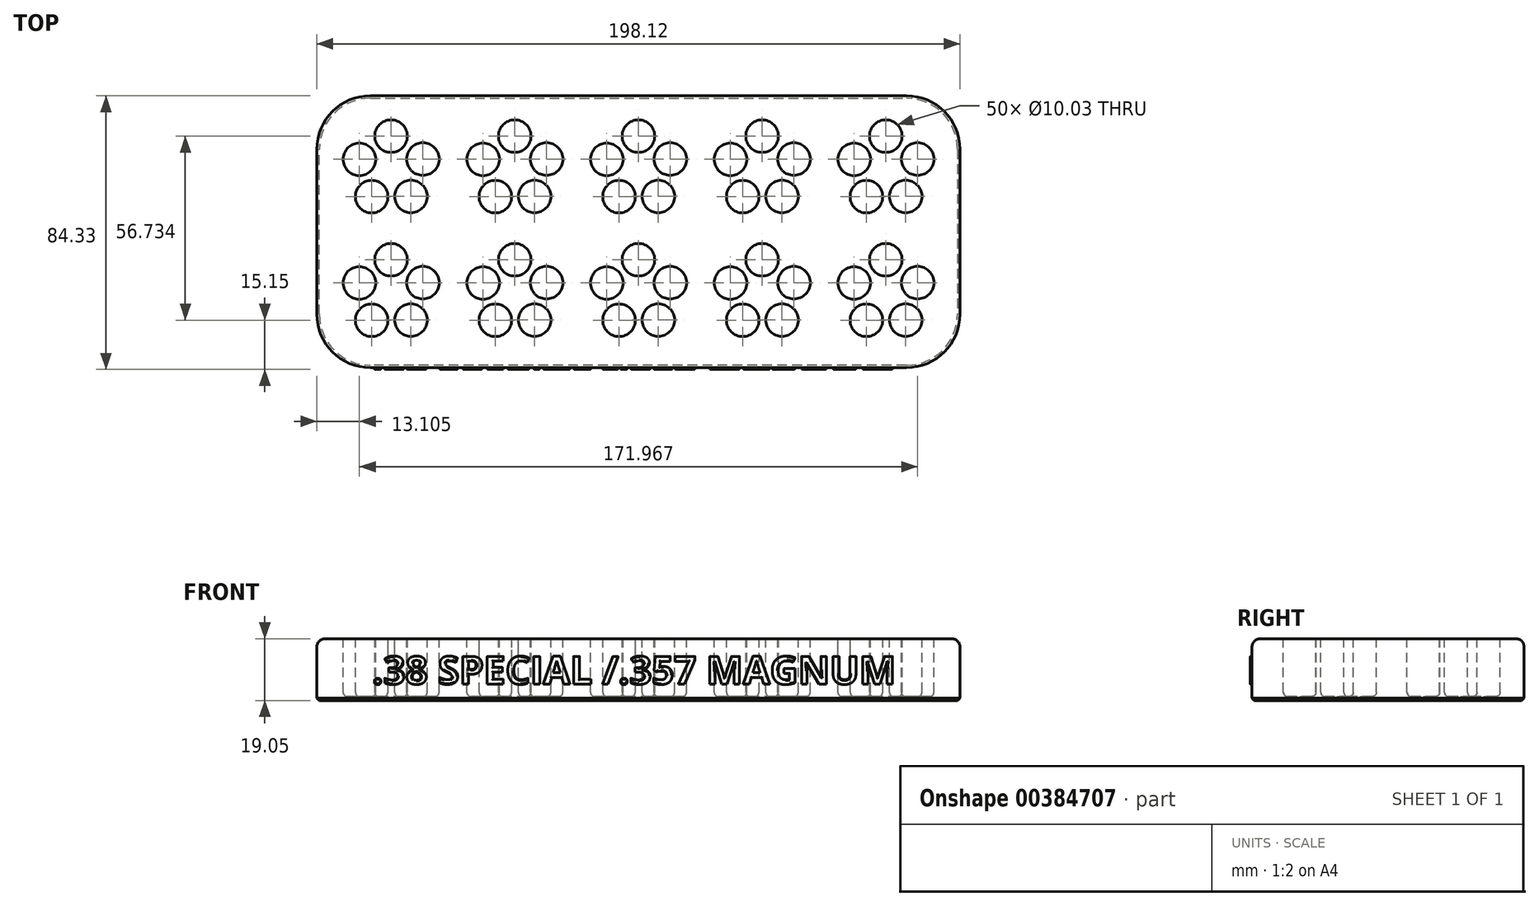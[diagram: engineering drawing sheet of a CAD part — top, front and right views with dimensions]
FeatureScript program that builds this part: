
annotation { "Feature Type Name" : "Feature", "Feature Type Description" : "" }
export const myFeature = defineFeature(function(context is Context, id is Id, definition is map)
    precondition{}
    {
        {
            var Q0;
            Q0=qCreatedBy(makeId("Top.planeOp"),FACE);
            var sketch = newSketch(context, id + "F0", { "sketchPlane" : qUnion([Q0])});
            skLineSegment(sketch, "E0.bottom", {"start": v(-96.52, 50.8) * mm, "end": v(101.6, 50.8) * mm});
            skLineSegment(sketch, "E0.top", {"start": v(-96.52, -33.02) * mm, "end": v(101.6, -33.02) * mm});
            skLineSegment(sketch, "E0.left", {"start": v(-96.52, 50.8) * mm, "end": v(-96.52, -33.02) * mm});
            skLineSegment(sketch, "E0.right", {"start": v(101.6, 50.8) * mm, "end": v(101.6, -33.02) * mm});
            skSolve(sketch);
        }
        {
            var Q0;
            Q0 = qSketchRegion(id + "F0", true);
            extrude(context, id + "F1", {"entities" : qUnion([Q0]), "depth" : 19.05 * mm});
        }
        {
            var Q0;
            Q0=makeQuery(id+"F1.opExtrude","CAP_FACE",FACE,{"disambiguationData":[OSD([sQuery(id+"F0.wireOp",EDGE,"E0.bottom"),sQuery(id+"F0.wireOp",EDGE,"E0.top"),sQuery(id+"F0.wireOp",EDGE,"E0.left"),sQuery(id+"F0.wireOp",EDGE,"E0.right")])],"isStart":false});
            var sketch = newSketch(context, id + "F2", { "sketchPlane" : qUnion([Q0])});
            skCircle(sketch, "E1", {"center": v(-73.66, 27.94) * mm, "radius": 16.83 * mm});
            skCircle(sketch, "E2", {"center": v(-73.66, -10.16) * mm, "radius": 16.83 * mm});
            skCircle(sketch, "E3.1.0.0", {"center": v(-35.56, -10.16) * mm, "radius": 16.83 * mm});
            skCircle(sketch, "E3.1.0.1", {"center": v(-35.56, 27.94) * mm, "radius": 16.83 * mm});
            skCircle(sketch, "E3.2.0.0", {"center": v(2.54, -10.16) * mm, "radius": 16.83 * mm});
            skCircle(sketch, "E3.2.0.1", {"center": v(2.54, 27.94) * mm, "radius": 16.83 * mm});
            skCircle(sketch, "E3.3.0.0", {"center": v(40.64, -10.16) * mm, "radius": 16.83 * mm});
            skCircle(sketch, "E3.3.0.1", {"center": v(40.64, 27.94) * mm, "radius": 16.83 * mm});
            skCircle(sketch, "E3.4.0.0", {"center": v(78.74, -10.16) * mm, "radius": 16.83 * mm});
            skCircle(sketch, "E3.4.0.1", {"center": v(78.74, 27.94) * mm, "radius": 16.83 * mm});
            skLineSegment(sketch, "E3.direction1", {"start": v(-73.66, -10.16) * mm, "end": v(-35.56, -10.16) * mm, "construction": true});
            skSolve(sketch);
        }
        {
            var Q0;
            Q0=makeQuery(id+"F2.imprint","IMPRINT",FACE,{"disambiguationData":[TD([[makeQuery(id+"F2.imprint","IMPRINT",EDGE,{"derivedFrom":sQuery(id+"F2.wireOp",EDGE,"E1")}),-1.0]])]});
            var sketch = newSketch(context, id + "F3", { "sketchPlane" : qUnion([Q0])});
            skCircle(sketch, "E4", {"center": v(-73.66, 38.35) * mm, "radius": 5.02 * mm});
            skCircle(sketch, "E5.1.0", {"center": v(-83.42, 31.2) * mm, "radius": 5.02 * mm});
            skCircle(sketch, "E5.2.0", {"center": v(-79.63, 19.72) * mm, "radius": 5.02 * mm});
            skCircle(sketch, "E5.3.0", {"center": v(-67.54, 19.77) * mm, "radius": 5.02 * mm});
            skCircle(sketch, "E5.4.0", {"center": v(-63.85, 31.29) * mm, "radius": 5.02 * mm});
            skPoint(sketch, "E5.center", {"position": v(-73.62, 28.07) * mm});
            skCircle(sketch, "E6.0.1.0", {"center": v(-79.63, -18.38) * mm, "radius": 5.02 * mm});
            skPoint(sketch, "E6.0.1.1", {"position": v(-73.62, -10.03) * mm});
            skCircle(sketch, "E6.0.1.2", {"center": v(-67.54, -18.33) * mm, "radius": 5.02 * mm});
            skCircle(sketch, "E6.0.1.3", {"center": v(-63.85, -6.81) * mm, "radius": 5.02 * mm});
            skCircle(sketch, "E6.0.1.4", {"center": v(-83.42, -6.9) * mm, "radius": 5.02 * mm});
            skCircle(sketch, "E6.0.1.5", {"center": v(-73.66, 0.25) * mm, "radius": 5.02 * mm});
            skCircle(sketch, "E6.1.0.0", {"center": v(-41.53, 19.72) * mm, "radius": 5.02 * mm});
            skPoint(sketch, "E6.1.0.1", {"position": v(-35.52, 28.07) * mm});
            skCircle(sketch, "E6.1.0.2", {"center": v(-29.44, 19.77) * mm, "radius": 5.02 * mm});
            skCircle(sketch, "E6.1.0.3", {"center": v(-25.75, 31.29) * mm, "radius": 5.02 * mm});
            skCircle(sketch, "E6.1.0.4", {"center": v(-45.32, 31.2) * mm, "radius": 5.02 * mm});
            skCircle(sketch, "E6.1.0.5", {"center": v(-35.56, 38.35) * mm, "radius": 5.02 * mm});
            skCircle(sketch, "E6.1.1.0", {"center": v(-41.53, -18.38) * mm, "radius": 5.02 * mm});
            skPoint(sketch, "E6.1.1.1", {"position": v(-35.52, -10.03) * mm});
            skCircle(sketch, "E6.1.1.2", {"center": v(-29.44, -18.33) * mm, "radius": 5.02 * mm});
            skCircle(sketch, "E6.1.1.3", {"center": v(-25.75, -6.81) * mm, "radius": 5.02 * mm});
            skCircle(sketch, "E6.1.1.4", {"center": v(-45.32, -6.9) * mm, "radius": 5.02 * mm});
            skCircle(sketch, "E6.1.1.5", {"center": v(-35.56, 0.25) * mm, "radius": 5.02 * mm});
            skCircle(sketch, "E6.2.0.0", {"center": v(-3.43, 19.72) * mm, "radius": 5.02 * mm});
            skPoint(sketch, "E6.2.0.1", {"position": v(2.58, 28.07) * mm});
            skCircle(sketch, "E6.2.0.2", {"center": v(8.66, 19.77) * mm, "radius": 5.02 * mm});
            skCircle(sketch, "E6.2.0.3", {"center": v(12.35, 31.29) * mm, "radius": 5.02 * mm});
            skCircle(sketch, "E6.2.0.4", {"center": v(-7.22, 31.2) * mm, "radius": 5.02 * mm});
            skCircle(sketch, "E6.2.0.5", {"center": v(2.54, 38.35) * mm, "radius": 5.02 * mm});
            skCircle(sketch, "E6.2.1.0", {"center": v(-3.43, -18.38) * mm, "radius": 5.02 * mm});
            skPoint(sketch, "E6.2.1.1", {"position": v(2.58, -10.03) * mm});
            skCircle(sketch, "E6.2.1.2", {"center": v(8.66, -18.33) * mm, "radius": 5.02 * mm});
            skCircle(sketch, "E6.2.1.3", {"center": v(12.35, -6.81) * mm, "radius": 5.02 * mm});
            skCircle(sketch, "E6.2.1.4", {"center": v(-7.22, -6.9) * mm, "radius": 5.02 * mm});
            skCircle(sketch, "E6.2.1.5", {"center": v(2.54, 0.25) * mm, "radius": 5.02 * mm});
            skCircle(sketch, "E6.3.0.0", {"center": v(34.67, 19.72) * mm, "radius": 5.02 * mm});
            skPoint(sketch, "E6.3.0.1", {"position": v(40.68, 28.07) * mm});
            skCircle(sketch, "E6.3.0.2", {"center": v(46.76, 19.77) * mm, "radius": 5.02 * mm});
            skCircle(sketch, "E6.3.0.3", {"center": v(50.45, 31.29) * mm, "radius": 5.02 * mm});
            skCircle(sketch, "E6.3.0.4", {"center": v(30.88, 31.2) * mm, "radius": 5.02 * mm});
            skCircle(sketch, "E6.3.0.5", {"center": v(40.64, 38.35) * mm, "radius": 5.02 * mm});
            skCircle(sketch, "E6.3.1.0", {"center": v(34.67, -18.38) * mm, "radius": 5.02 * mm});
            skPoint(sketch, "E6.3.1.1", {"position": v(40.68, -10.03) * mm});
            skCircle(sketch, "E6.3.1.2", {"center": v(46.76, -18.33) * mm, "radius": 5.02 * mm});
            skCircle(sketch, "E6.3.1.3", {"center": v(50.45, -6.81) * mm, "radius": 5.02 * mm});
            skCircle(sketch, "E6.3.1.4", {"center": v(30.88, -6.9) * mm, "radius": 5.02 * mm});
            skCircle(sketch, "E6.3.1.5", {"center": v(40.64, 0.25) * mm, "radius": 5.02 * mm});
            skCircle(sketch, "E6.4.0.0", {"center": v(72.77, 19.72) * mm, "radius": 5.02 * mm});
            skPoint(sketch, "E6.4.0.1", {"position": v(78.78, 28.07) * mm});
            skCircle(sketch, "E6.4.0.2", {"center": v(84.86, 19.77) * mm, "radius": 5.02 * mm});
            skCircle(sketch, "E6.4.0.3", {"center": v(88.55, 31.29) * mm, "radius": 5.02 * mm});
            skCircle(sketch, "E6.4.0.4", {"center": v(68.98, 31.2) * mm, "radius": 5.02 * mm});
            skCircle(sketch, "E6.4.0.5", {"center": v(78.74, 38.35) * mm, "radius": 5.02 * mm});
            skCircle(sketch, "E6.4.1.0", {"center": v(72.77, -18.38) * mm, "radius": 5.02 * mm});
            skPoint(sketch, "E6.4.1.1", {"position": v(78.78, -10.03) * mm});
            skCircle(sketch, "E6.4.1.2", {"center": v(84.86, -18.33) * mm, "radius": 5.02 * mm});
            skCircle(sketch, "E6.4.1.3", {"center": v(88.55, -6.81) * mm, "radius": 5.02 * mm});
            skCircle(sketch, "E6.4.1.4", {"center": v(68.98, -6.9) * mm, "radius": 5.02 * mm});
            skCircle(sketch, "E6.4.1.5", {"center": v(78.74, 0.25) * mm, "radius": 5.02 * mm});
            skLineSegment(sketch, "E6.direction1", {"start": v(-79.63, 19.72) * mm, "end": v(-41.53, 19.72) * mm, "construction": true});
            skLineSegment(sketch, "E6.direction2", {"start": v(-79.63, 19.72) * mm, "end": v(-79.63, -18.38) * mm, "construction": true});
            skSolve(sketch);
        }
        {
            var Q0;
            Q0 = qSketchRegion(id + "F3", true);
            extrude(context, id + "F4", {"entities" : qUnion([Q0]), "operationType" : NewBodyOperationType.REMOVE, "oppositeDirection" : true, "depth" : 17.78 * mm});
        }
        {
            var Q0;
            Q0=makeQuery(id+"F1.opExtrude","SWEPT_EDGE",EDGE,{"disambiguationData":[OSD([sQuery(id+"F0.wireOp",EDGE,"E0.top"),sQuery(id+"F0.wireOp",EDGE,"E0.left")])]});
            var Q1;
            Q1=makeQuery(id+"F1.opExtrude","SWEPT_EDGE",EDGE,{"disambiguationData":[OSD([sQuery(id+"F0.wireOp",EDGE,"E0.bottom"),sQuery(id+"F0.wireOp",EDGE,"E0.left")])]});
            var Q2;
            Q2=makeQuery(id+"F1.opExtrude","SWEPT_EDGE",EDGE,{"disambiguationData":[OSD([sQuery(id+"F0.wireOp",EDGE,"E0.bottom"),sQuery(id+"F0.wireOp",EDGE,"E0.right")])]});
            var Q3;
            Q3=makeQuery(id+"F1.opExtrude","SWEPT_EDGE",EDGE,{"disambiguationData":[OSD([sQuery(id+"F0.wireOp",EDGE,"E0.top"),sQuery(id+"F0.wireOp",EDGE,"E0.right")])]});
            fillet(context, id + "F5", {"entities" : qUnion([Q0, Q1, Q2, Q3]), "radius" : 16.5 * mm, "tangentPropagation" : true, "allowEdgeOverflow" : false});
        }
        {
            var Q0;
            Q0=makeQuery(id+"F1.opExtrude","CAP_EDGE",EDGE,{"disambiguationData":[OSD([sQuery(id+"F0.wireOp",EDGE,"E0.bottom")])],"isStart":false});
            fillet(context, id + "F6", {"entities" : qUnion([Q0]), "radius" : 2.54 * mm, "tangentPropagation" : true, "allowEdgeOverflow" : false});
        }
        {
            var Q0;
            Q0=makeQuery(id+"F4.boolean.opBoolean","COPY",EDGE,{"derivedFrom":makeQuery(id+"F4.opExtrude","CAP_EDGE",EDGE,{"disambiguationData":[OSD([sQuery(id+"F3.wireOp",EDGE,"E6.2.0.3")])],"isStart":true})});
            var Q1;
            Q1=makeQuery(id+"F4.boolean.opBoolean","COPY",EDGE,{"derivedFrom":makeQuery(id+"F4.opExtrude","CAP_EDGE",EDGE,{"disambiguationData":[OSD([sQuery(id+"F3.wireOp",EDGE,"E6.1.0.3")])],"isStart":true})});
            var Q2;
            Q2=makeQuery(id+"F4.boolean.opBoolean","COPY",EDGE,{"derivedFrom":makeQuery(id+"F4.opExtrude","CAP_EDGE",EDGE,{"disambiguationData":[OSD([sQuery(id+"F3.wireOp",EDGE,"E6.4.0.3")])],"isStart":true})});
            var Q3;
            Q3=makeQuery(id+"F4.boolean.opBoolean","COPY",EDGE,{"derivedFrom":makeQuery(id+"F4.opExtrude","CAP_EDGE",EDGE,{"disambiguationData":[OSD([sQuery(id+"F3.wireOp",EDGE,"E6.4.1.0")])],"isStart":true})});
            var Q4;
            Q4=makeQuery(id+"F4.boolean.opBoolean","COPY",EDGE,{"derivedFrom":makeQuery(id+"F4.opExtrude","CAP_EDGE",EDGE,{"disambiguationData":[OSD([sQuery(id+"F3.wireOp",EDGE,"E6.4.0.2")])],"isStart":true})});
            var Q5;
            Q5=makeQuery(id+"F4.boolean.opBoolean","COPY",EDGE,{"derivedFrom":makeQuery(id+"F4.opExtrude","CAP_EDGE",EDGE,{"disambiguationData":[OSD([sQuery(id+"F3.wireOp",EDGE,"E6.4.0.0")])],"isStart":true})});
            var Q6;
            Q6=makeQuery(id+"F4.boolean.opBoolean","COPY",EDGE,{"derivedFrom":makeQuery(id+"F4.opExtrude","CAP_EDGE",EDGE,{"disambiguationData":[OSD([sQuery(id+"F3.wireOp",EDGE,"E6.0.1.5")])],"isStart":true})});
            var Q7;
            Q7=makeQuery(id+"F4.boolean.opBoolean","COPY",EDGE,{"derivedFrom":makeQuery(id+"F4.opExtrude","CAP_EDGE",EDGE,{"disambiguationData":[OSD([sQuery(id+"F3.wireOp",EDGE,"E6.2.0.0")])],"isStart":true})});
            var Q8;
            Q8=makeQuery(id+"F4.boolean.opBoolean","COPY",EDGE,{"derivedFrom":makeQuery(id+"F4.opExtrude","CAP_EDGE",EDGE,{"disambiguationData":[OSD([sQuery(id+"F3.wireOp",EDGE,"E4")])],"isStart":true})});
            var Q9;
            Q9=makeQuery(id+"F4.boolean.opBoolean","COPY",EDGE,{"derivedFrom":makeQuery(id+"F4.opExtrude","CAP_EDGE",EDGE,{"disambiguationData":[OSD([sQuery(id+"F3.wireOp",EDGE,"E6.2.1.0")])],"isStart":true})});
            var Q10;
            Q10=makeQuery(id+"F4.boolean.opBoolean","COPY",EDGE,{"derivedFrom":makeQuery(id+"F4.opExtrude","CAP_EDGE",EDGE,{"disambiguationData":[OSD([sQuery(id+"F3.wireOp",EDGE,"E6.1.1.3")])],"isStart":true})});
            var Q11;
            Q11=makeQuery(id+"F4.boolean.opBoolean","COPY",EDGE,{"derivedFrom":makeQuery(id+"F4.opExtrude","CAP_EDGE",EDGE,{"disambiguationData":[OSD([sQuery(id+"F3.wireOp",EDGE,"E6.2.1.2")])],"isStart":true})});
            var Q12;
            Q12=makeQuery(id+"F4.boolean.opBoolean","COPY",EDGE,{"derivedFrom":makeQuery(id+"F4.opExtrude","CAP_EDGE",EDGE,{"disambiguationData":[OSD([sQuery(id+"F3.wireOp",EDGE,"E5.4.0")])],"isStart":true})});
            var Q13;
            Q13=makeQuery(id+"F4.boolean.opBoolean","COPY",EDGE,{"derivedFrom":makeQuery(id+"F4.opExtrude","CAP_EDGE",EDGE,{"disambiguationData":[OSD([sQuery(id+"F3.wireOp",EDGE,"E5.3.0")])],"isStart":true})});
            var Q14;
            Q14=makeQuery(id+"F4.boolean.opBoolean","COPY",EDGE,{"derivedFrom":makeQuery(id+"F4.opExtrude","CAP_EDGE",EDGE,{"disambiguationData":[OSD([sQuery(id+"F3.wireOp",EDGE,"E6.3.1.4")])],"isStart":true})});
            var Q15;
            Q15=makeQuery(id+"F4.boolean.opBoolean","COPY",EDGE,{"derivedFrom":makeQuery(id+"F4.opExtrude","CAP_EDGE",EDGE,{"disambiguationData":[OSD([sQuery(id+"F3.wireOp",EDGE,"E6.1.0.5")])],"isStart":true})});
            var Q16;
            Q16=makeQuery(id+"F4.boolean.opBoolean","COPY",EDGE,{"derivedFrom":makeQuery(id+"F4.opExtrude","CAP_EDGE",EDGE,{"disambiguationData":[OSD([sQuery(id+"F3.wireOp",EDGE,"E6.1.0.4")])],"isStart":true})});
            var Q17;
            Q17=makeQuery(id+"F4.boolean.opBoolean","COPY",EDGE,{"derivedFrom":makeQuery(id+"F4.opExtrude","CAP_EDGE",EDGE,{"disambiguationData":[OSD([sQuery(id+"F3.wireOp",EDGE,"E6.2.1.3")])],"isStart":true})});
            var Q18;
            Q18=makeQuery(id+"F4.boolean.opBoolean","COPY",EDGE,{"derivedFrom":makeQuery(id+"F4.opExtrude","CAP_EDGE",EDGE,{"disambiguationData":[OSD([sQuery(id+"F3.wireOp",EDGE,"E6.1.1.4")])],"isStart":true})});
            var Q19;
            Q19=makeQuery(id+"F4.boolean.opBoolean","COPY",EDGE,{"derivedFrom":makeQuery(id+"F4.opExtrude","CAP_EDGE",EDGE,{"disambiguationData":[OSD([sQuery(id+"F3.wireOp",EDGE,"E6.3.0.2")])],"isStart":true})});
            var Q20;
            Q20=makeQuery(id+"F4.boolean.opBoolean","COPY",EDGE,{"derivedFrom":makeQuery(id+"F4.opExtrude","CAP_EDGE",EDGE,{"disambiguationData":[OSD([sQuery(id+"F3.wireOp",EDGE,"E6.3.1.5")])],"isStart":true})});
            var Q21;
            Q21=makeQuery(id+"F4.boolean.opBoolean","COPY",EDGE,{"derivedFrom":makeQuery(id+"F4.opExtrude","CAP_EDGE",EDGE,{"disambiguationData":[OSD([sQuery(id+"F3.wireOp",EDGE,"E6.4.1.3")])],"isStart":true})});
            var Q22;
            Q22=makeQuery(id+"F4.boolean.opBoolean","COPY",EDGE,{"derivedFrom":makeQuery(id+"F4.opExtrude","CAP_EDGE",EDGE,{"disambiguationData":[OSD([sQuery(id+"F3.wireOp",EDGE,"E6.2.1.5")])],"isStart":true})});
            var Q23;
            Q23=makeQuery(id+"F4.boolean.opBoolean","COPY",EDGE,{"derivedFrom":makeQuery(id+"F4.opExtrude","CAP_EDGE",EDGE,{"disambiguationData":[OSD([sQuery(id+"F3.wireOp",EDGE,"E6.4.1.2")])],"isStart":true})});
            var Q24;
            Q24=makeQuery(id+"F4.boolean.opBoolean","COPY",EDGE,{"derivedFrom":makeQuery(id+"F4.opExtrude","CAP_EDGE",EDGE,{"disambiguationData":[OSD([sQuery(id+"F3.wireOp",EDGE,"E6.2.0.2")])],"isStart":true})});
            var Q25;
            Q25=makeQuery(id+"F4.boolean.opBoolean","COPY",EDGE,{"derivedFrom":makeQuery(id+"F4.opExtrude","CAP_EDGE",EDGE,{"disambiguationData":[OSD([sQuery(id+"F3.wireOp",EDGE,"E6.1.1.5")])],"isStart":true})});
            var Q26;
            Q26=makeQuery(id+"F4.boolean.opBoolean","COPY",EDGE,{"derivedFrom":makeQuery(id+"F4.opExtrude","CAP_EDGE",EDGE,{"disambiguationData":[OSD([sQuery(id+"F3.wireOp",EDGE,"E6.3.0.0")])],"isStart":true})});
            var Q27;
            Q27=makeQuery(id+"F4.boolean.opBoolean","COPY",EDGE,{"derivedFrom":makeQuery(id+"F4.opExtrude","CAP_EDGE",EDGE,{"disambiguationData":[OSD([sQuery(id+"F3.wireOp",EDGE,"E6.2.0.5")])],"isStart":true})});
            var Q28;
            Q28=makeQuery(id+"F4.boolean.opBoolean","COPY",EDGE,{"derivedFrom":makeQuery(id+"F4.opExtrude","CAP_EDGE",EDGE,{"disambiguationData":[OSD([sQuery(id+"F3.wireOp",EDGE,"E6.0.1.0")])],"isStart":true})});
            var Q29;
            Q29=makeQuery(id+"F4.boolean.opBoolean","COPY",EDGE,{"derivedFrom":makeQuery(id+"F4.opExtrude","CAP_EDGE",EDGE,{"disambiguationData":[OSD([sQuery(id+"F3.wireOp",EDGE,"E6.4.0.4")])],"isStart":true})});
            var Q30;
            Q30=makeQuery(id+"F4.boolean.opBoolean","COPY",EDGE,{"derivedFrom":makeQuery(id+"F4.opExtrude","CAP_EDGE",EDGE,{"disambiguationData":[OSD([sQuery(id+"F3.wireOp",EDGE,"E6.4.0.5")])],"isStart":true})});
            var Q31;
            Q31=makeQuery(id+"F4.boolean.opBoolean","COPY",EDGE,{"derivedFrom":makeQuery(id+"F4.opExtrude","CAP_EDGE",EDGE,{"disambiguationData":[OSD([sQuery(id+"F3.wireOp",EDGE,"E6.3.0.3")])],"isStart":true})});
            var Q32;
            Q32=makeQuery(id+"F4.boolean.opBoolean","COPY",EDGE,{"derivedFrom":makeQuery(id+"F4.opExtrude","CAP_EDGE",EDGE,{"disambiguationData":[OSD([sQuery(id+"F3.wireOp",EDGE,"E6.4.1.4")])],"isStart":true})});
            var Q33;
            Q33=makeQuery(id+"F4.boolean.opBoolean","COPY",EDGE,{"derivedFrom":makeQuery(id+"F4.opExtrude","CAP_EDGE",EDGE,{"disambiguationData":[OSD([sQuery(id+"F3.wireOp",EDGE,"E6.3.1.2")])],"isStart":true})});
            var Q34;
            Q34=makeQuery(id+"F4.boolean.opBoolean","COPY",EDGE,{"derivedFrom":makeQuery(id+"F4.opExtrude","CAP_EDGE",EDGE,{"disambiguationData":[OSD([sQuery(id+"F3.wireOp",EDGE,"E5.2.0")])],"isStart":true})});
            var Q35;
            Q35=makeQuery(id+"F4.boolean.opBoolean","COPY",EDGE,{"derivedFrom":makeQuery(id+"F4.opExtrude","CAP_EDGE",EDGE,{"disambiguationData":[OSD([sQuery(id+"F3.wireOp",EDGE,"E6.0.1.2")])],"isStart":true})});
            var Q36;
            Q36=makeQuery(id+"F4.boolean.opBoolean","COPY",EDGE,{"derivedFrom":makeQuery(id+"F4.opExtrude","CAP_EDGE",EDGE,{"disambiguationData":[OSD([sQuery(id+"F3.wireOp",EDGE,"E6.1.0.2")])],"isStart":true})});
            var Q37;
            Q37=makeQuery(id+"F4.boolean.opBoolean","COPY",EDGE,{"derivedFrom":makeQuery(id+"F4.opExtrude","CAP_EDGE",EDGE,{"disambiguationData":[OSD([sQuery(id+"F3.wireOp",EDGE,"E6.1.1.0")])],"isStart":true})});
            var Q38;
            Q38=makeQuery(id+"F4.boolean.opBoolean","COPY",EDGE,{"derivedFrom":makeQuery(id+"F4.opExtrude","CAP_EDGE",EDGE,{"disambiguationData":[OSD([sQuery(id+"F3.wireOp",EDGE,"E6.2.0.4")])],"isStart":true})});
            var Q39;
            Q39=makeQuery(id+"F4.boolean.opBoolean","COPY",EDGE,{"derivedFrom":makeQuery(id+"F4.opExtrude","CAP_EDGE",EDGE,{"disambiguationData":[OSD([sQuery(id+"F3.wireOp",EDGE,"E6.2.1.4")])],"isStart":true})});
            var Q40;
            Q40=makeQuery(id+"F4.boolean.opBoolean","COPY",EDGE,{"derivedFrom":makeQuery(id+"F4.opExtrude","CAP_EDGE",EDGE,{"disambiguationData":[OSD([sQuery(id+"F3.wireOp",EDGE,"E6.1.0.0")])],"isStart":true})});
            var Q41;
            Q41=makeQuery(id+"F4.boolean.opBoolean","COPY",EDGE,{"derivedFrom":makeQuery(id+"F4.opExtrude","CAP_EDGE",EDGE,{"disambiguationData":[OSD([sQuery(id+"F3.wireOp",EDGE,"E6.1.1.2")])],"isStart":true})});
            var Q42;
            Q42=makeQuery(id+"F4.boolean.opBoolean","COPY",EDGE,{"derivedFrom":makeQuery(id+"F4.opExtrude","CAP_EDGE",EDGE,{"disambiguationData":[OSD([sQuery(id+"F3.wireOp",EDGE,"E6.0.1.3")])],"isStart":true})});
            var Q43;
            Q43=makeQuery(id+"F4.boolean.opBoolean","COPY",EDGE,{"derivedFrom":makeQuery(id+"F4.opExtrude","CAP_EDGE",EDGE,{"disambiguationData":[OSD([sQuery(id+"F3.wireOp",EDGE,"E6.4.1.5")])],"isStart":true})});
            var Q44;
            Q44=makeQuery(id+"F4.boolean.opBoolean","COPY",EDGE,{"derivedFrom":makeQuery(id+"F4.opExtrude","CAP_EDGE",EDGE,{"disambiguationData":[OSD([sQuery(id+"F3.wireOp",EDGE,"E6.3.0.4")])],"isStart":true})});
            var Q45;
            Q45=makeQuery(id+"F4.boolean.opBoolean","COPY",EDGE,{"derivedFrom":makeQuery(id+"F4.opExtrude","CAP_EDGE",EDGE,{"disambiguationData":[OSD([sQuery(id+"F3.wireOp",EDGE,"E6.3.0.5")])],"isStart":true})});
            var Q46;
            Q46=makeQuery(id+"F4.boolean.opBoolean","COPY",EDGE,{"derivedFrom":makeQuery(id+"F4.opExtrude","CAP_EDGE",EDGE,{"disambiguationData":[OSD([sQuery(id+"F3.wireOp",EDGE,"E6.3.1.0")])],"isStart":true})});
            var Q47;
            Q47=makeQuery(id+"F4.boolean.opBoolean","COPY",EDGE,{"derivedFrom":makeQuery(id+"F4.opExtrude","CAP_EDGE",EDGE,{"disambiguationData":[OSD([sQuery(id+"F3.wireOp",EDGE,"E6.3.1.3")])],"isStart":true})});
            var Q48;
            Q48=makeQuery(id+"F4.boolean.opBoolean","COPY",EDGE,{"derivedFrom":makeQuery(id+"F4.opExtrude","CAP_EDGE",EDGE,{"disambiguationData":[OSD([sQuery(id+"F3.wireOp",EDGE,"E6.0.1.2")])],"isStart":false})});
            var Q49;
            Q49=makeQuery(id+"F4.boolean.opBoolean","COPY",EDGE,{"derivedFrom":makeQuery(id+"F4.opExtrude","CAP_EDGE",EDGE,{"disambiguationData":[OSD([sQuery(id+"F3.wireOp",EDGE,"E6.0.1.3")])],"isStart":false})});
            var Q50;
            Q50=makeQuery(id+"F4.boolean.opBoolean","COPY",EDGE,{"derivedFrom":makeQuery(id+"F4.opExtrude","CAP_EDGE",EDGE,{"disambiguationData":[OSD([sQuery(id+"F3.wireOp",EDGE,"E4")])],"isStart":false})});
            var Q51;
            Q51=makeQuery(id+"F4.boolean.opBoolean","COPY",EDGE,{"derivedFrom":makeQuery(id+"F4.opExtrude","CAP_EDGE",EDGE,{"disambiguationData":[OSD([sQuery(id+"F3.wireOp",EDGE,"E5.2.0")])],"isStart":false})});
            var Q52;
            Q52=makeQuery(id+"F4.boolean.opBoolean","COPY",EDGE,{"derivedFrom":makeQuery(id+"F4.opExtrude","CAP_EDGE",EDGE,{"disambiguationData":[OSD([sQuery(id+"F3.wireOp",EDGE,"E5.3.0")])],"isStart":false})});
            var Q53;
            Q53=makeQuery(id+"F4.boolean.opBoolean","COPY",EDGE,{"derivedFrom":makeQuery(id+"F4.opExtrude","CAP_EDGE",EDGE,{"disambiguationData":[OSD([sQuery(id+"F3.wireOp",EDGE,"E5.4.0")])],"isStart":false})});
            var Q54;
            Q54=makeQuery(id+"F4.boolean.opBoolean","COPY",EDGE,{"derivedFrom":makeQuery(id+"F4.opExtrude","CAP_EDGE",EDGE,{"disambiguationData":[OSD([sQuery(id+"F3.wireOp",EDGE,"E6.0.1.0")])],"isStart":false})});
            var Q55;
            Q55=makeQuery(id+"F4.boolean.opBoolean","COPY",EDGE,{"derivedFrom":makeQuery(id+"F4.opExtrude","CAP_EDGE",EDGE,{"disambiguationData":[OSD([sQuery(id+"F3.wireOp",EDGE,"E6.1.0.5")])],"isStart":false})});
            var Q56;
            Q56=makeQuery(id+"F4.boolean.opBoolean","COPY",EDGE,{"derivedFrom":makeQuery(id+"F4.opExtrude","CAP_EDGE",EDGE,{"disambiguationData":[OSD([sQuery(id+"F3.wireOp",EDGE,"E6.2.0.3")])],"isStart":false})});
            var Q57;
            Q57=makeQuery(id+"F4.boolean.opBoolean","COPY",EDGE,{"derivedFrom":makeQuery(id+"F4.opExtrude","CAP_EDGE",EDGE,{"disambiguationData":[OSD([sQuery(id+"F3.wireOp",EDGE,"E6.3.0.0")])],"isStart":false})});
            var Q58;
            Q58=makeQuery(id+"F4.boolean.opBoolean","COPY",EDGE,{"derivedFrom":makeQuery(id+"F4.opExtrude","CAP_EDGE",EDGE,{"disambiguationData":[OSD([sQuery(id+"F3.wireOp",EDGE,"E6.3.1.4")])],"isStart":false})});
            var Q59;
            Q59=makeQuery(id+"F4.boolean.opBoolean","COPY",EDGE,{"derivedFrom":makeQuery(id+"F4.opExtrude","CAP_EDGE",EDGE,{"disambiguationData":[OSD([sQuery(id+"F3.wireOp",EDGE,"E6.4.1.2")])],"isStart":false})});
            var Q60;
            Q60=makeQuery(id+"F4.boolean.opBoolean","COPY",EDGE,{"derivedFrom":makeQuery(id+"F4.opExtrude","CAP_EDGE",EDGE,{"disambiguationData":[OSD([sQuery(id+"F3.wireOp",EDGE,"E6.1.1.0")])],"isStart":false})});
            var Q61;
            Q61=makeQuery(id+"F4.boolean.opBoolean","COPY",EDGE,{"derivedFrom":makeQuery(id+"F4.opExtrude","CAP_EDGE",EDGE,{"disambiguationData":[OSD([sQuery(id+"F3.wireOp",EDGE,"E6.2.0.4")])],"isStart":false})});
            var Q62;
            Q62=makeQuery(id+"F4.boolean.opBoolean","COPY",EDGE,{"derivedFrom":makeQuery(id+"F4.opExtrude","CAP_EDGE",EDGE,{"disambiguationData":[OSD([sQuery(id+"F3.wireOp",EDGE,"E6.3.0.2")])],"isStart":false})});
            var Q63;
            Q63=makeQuery(id+"F4.boolean.opBoolean","COPY",EDGE,{"derivedFrom":makeQuery(id+"F4.opExtrude","CAP_EDGE",EDGE,{"disambiguationData":[OSD([sQuery(id+"F3.wireOp",EDGE,"E6.3.1.5")])],"isStart":false})});
            var Q64;
            Q64=makeQuery(id+"F4.boolean.opBoolean","COPY",EDGE,{"derivedFrom":makeQuery(id+"F4.opExtrude","CAP_EDGE",EDGE,{"disambiguationData":[OSD([sQuery(id+"F3.wireOp",EDGE,"E6.4.1.3")])],"isStart":false})});
            var Q65;
            Q65=makeQuery(id+"F4.boolean.opBoolean","COPY",EDGE,{"derivedFrom":makeQuery(id+"F4.opExtrude","CAP_EDGE",EDGE,{"disambiguationData":[OSD([sQuery(id+"F3.wireOp",EDGE,"E6.1.1.2")])],"isStart":false})});
            var Q66;
            Q66=makeQuery(id+"F4.boolean.opBoolean","COPY",EDGE,{"derivedFrom":makeQuery(id+"F4.opExtrude","CAP_EDGE",EDGE,{"disambiguationData":[OSD([sQuery(id+"F3.wireOp",EDGE,"E6.2.0.5")])],"isStart":false})});
            var Q67;
            Q67=makeQuery(id+"F4.boolean.opBoolean","COPY",EDGE,{"derivedFrom":makeQuery(id+"F4.opExtrude","CAP_EDGE",EDGE,{"disambiguationData":[OSD([sQuery(id+"F3.wireOp",EDGE,"E6.3.0.3")])],"isStart":false})});
            var Q68;
            Q68=makeQuery(id+"F4.boolean.opBoolean","COPY",EDGE,{"derivedFrom":makeQuery(id+"F4.opExtrude","CAP_EDGE",EDGE,{"disambiguationData":[OSD([sQuery(id+"F3.wireOp",EDGE,"E6.4.0.0")])],"isStart":false})});
            var Q69;
            Q69=makeQuery(id+"F4.boolean.opBoolean","COPY",EDGE,{"derivedFrom":makeQuery(id+"F4.opExtrude","CAP_EDGE",EDGE,{"disambiguationData":[OSD([sQuery(id+"F3.wireOp",EDGE,"E6.4.1.4")])],"isStart":false})});
            var Q70;
            Q70=makeQuery(id+"F4.boolean.opBoolean","COPY",EDGE,{"derivedFrom":makeQuery(id+"F4.opExtrude","CAP_EDGE",EDGE,{"disambiguationData":[OSD([sQuery(id+"F3.wireOp",EDGE,"E6.0.1.5")])],"isStart":false})});
            var Q71;
            Q71=makeQuery(id+"F4.boolean.opBoolean","COPY",EDGE,{"derivedFrom":makeQuery(id+"F4.opExtrude","CAP_EDGE",EDGE,{"disambiguationData":[OSD([sQuery(id+"F3.wireOp",EDGE,"E6.1.1.3")])],"isStart":false})});
            var Q72;
            Q72=makeQuery(id+"F4.boolean.opBoolean","COPY",EDGE,{"derivedFrom":makeQuery(id+"F4.opExtrude","CAP_EDGE",EDGE,{"disambiguationData":[OSD([sQuery(id+"F3.wireOp",EDGE,"E6.2.1.0")])],"isStart":false})});
            var Q73;
            Q73=makeQuery(id+"F4.boolean.opBoolean","COPY",EDGE,{"derivedFrom":makeQuery(id+"F4.opExtrude","CAP_EDGE",EDGE,{"disambiguationData":[OSD([sQuery(id+"F3.wireOp",EDGE,"E6.3.0.4")])],"isStart":false})});
            var Q74;
            Q74=makeQuery(id+"F4.boolean.opBoolean","COPY",EDGE,{"derivedFrom":makeQuery(id+"F4.opExtrude","CAP_EDGE",EDGE,{"disambiguationData":[OSD([sQuery(id+"F3.wireOp",EDGE,"E6.4.0.2")])],"isStart":false})});
            var Q75;
            Q75=makeQuery(id+"F4.boolean.opBoolean","COPY",EDGE,{"derivedFrom":makeQuery(id+"F4.opExtrude","CAP_EDGE",EDGE,{"disambiguationData":[OSD([sQuery(id+"F3.wireOp",EDGE,"E6.4.1.5")])],"isStart":false})});
            var Q76;
            Q76=makeQuery(id+"F4.boolean.opBoolean","COPY",EDGE,{"derivedFrom":makeQuery(id+"F4.opExtrude","CAP_EDGE",EDGE,{"disambiguationData":[OSD([sQuery(id+"F3.wireOp",EDGE,"E6.1.0.0")])],"isStart":false})});
            var Q77;
            Q77=makeQuery(id+"F4.boolean.opBoolean","COPY",EDGE,{"derivedFrom":makeQuery(id+"F4.opExtrude","CAP_EDGE",EDGE,{"disambiguationData":[OSD([sQuery(id+"F3.wireOp",EDGE,"E6.1.1.4")])],"isStart":false})});
            var Q78;
            Q78=makeQuery(id+"F4.boolean.opBoolean","COPY",EDGE,{"derivedFrom":makeQuery(id+"F4.opExtrude","CAP_EDGE",EDGE,{"disambiguationData":[OSD([sQuery(id+"F3.wireOp",EDGE,"E6.2.1.2")])],"isStart":false})});
            var Q79;
            Q79=makeQuery(id+"F4.boolean.opBoolean","COPY",EDGE,{"derivedFrom":makeQuery(id+"F4.opExtrude","CAP_EDGE",EDGE,{"disambiguationData":[OSD([sQuery(id+"F3.wireOp",EDGE,"E6.3.0.5")])],"isStart":false})});
            var Q80;
            Q80=makeQuery(id+"F4.boolean.opBoolean","COPY",EDGE,{"derivedFrom":makeQuery(id+"F4.opExtrude","CAP_EDGE",EDGE,{"disambiguationData":[OSD([sQuery(id+"F3.wireOp",EDGE,"E6.4.0.3")])],"isStart":false})});
            var Q81;
            Q81=makeQuery(id+"F4.boolean.opBoolean","COPY",EDGE,{"derivedFrom":makeQuery(id+"F4.opExtrude","CAP_EDGE",EDGE,{"disambiguationData":[OSD([sQuery(id+"F3.wireOp",EDGE,"E6.1.0.2")])],"isStart":false})});
            var Q82;
            Q82=makeQuery(id+"F4.boolean.opBoolean","COPY",EDGE,{"derivedFrom":makeQuery(id+"F4.opExtrude","CAP_EDGE",EDGE,{"disambiguationData":[OSD([sQuery(id+"F3.wireOp",EDGE,"E6.1.1.5")])],"isStart":false})});
            var Q83;
            Q83=makeQuery(id+"F4.boolean.opBoolean","COPY",EDGE,{"derivedFrom":makeQuery(id+"F4.opExtrude","CAP_EDGE",EDGE,{"disambiguationData":[OSD([sQuery(id+"F3.wireOp",EDGE,"E6.2.1.3")])],"isStart":false})});
            var Q84;
            Q84=makeQuery(id+"F4.boolean.opBoolean","COPY",EDGE,{"derivedFrom":makeQuery(id+"F4.opExtrude","CAP_EDGE",EDGE,{"disambiguationData":[OSD([sQuery(id+"F3.wireOp",EDGE,"E6.3.1.0")])],"isStart":false})});
            var Q85;
            Q85=makeQuery(id+"F4.boolean.opBoolean","COPY",EDGE,{"derivedFrom":makeQuery(id+"F4.opExtrude","CAP_EDGE",EDGE,{"disambiguationData":[OSD([sQuery(id+"F3.wireOp",EDGE,"E6.4.0.4")])],"isStart":false})});
            var Q86;
            Q86=makeQuery(id+"F4.boolean.opBoolean","COPY",EDGE,{"derivedFrom":makeQuery(id+"F4.opExtrude","CAP_EDGE",EDGE,{"disambiguationData":[OSD([sQuery(id+"F3.wireOp",EDGE,"E6.1.0.3")])],"isStart":false})});
            var Q87;
            Q87=makeQuery(id+"F4.boolean.opBoolean","COPY",EDGE,{"derivedFrom":makeQuery(id+"F4.opExtrude","CAP_EDGE",EDGE,{"disambiguationData":[OSD([sQuery(id+"F3.wireOp",EDGE,"E6.2.0.0")])],"isStart":false})});
            var Q88;
            Q88=makeQuery(id+"F4.boolean.opBoolean","COPY",EDGE,{"derivedFrom":makeQuery(id+"F4.opExtrude","CAP_EDGE",EDGE,{"disambiguationData":[OSD([sQuery(id+"F3.wireOp",EDGE,"E6.2.1.4")])],"isStart":false})});
            var Q89;
            Q89=makeQuery(id+"F4.boolean.opBoolean","COPY",EDGE,{"derivedFrom":makeQuery(id+"F4.opExtrude","CAP_EDGE",EDGE,{"disambiguationData":[OSD([sQuery(id+"F3.wireOp",EDGE,"E6.3.1.2")])],"isStart":false})});
            var Q90;
            Q90=makeQuery(id+"F4.boolean.opBoolean","COPY",EDGE,{"derivedFrom":makeQuery(id+"F4.opExtrude","CAP_EDGE",EDGE,{"disambiguationData":[OSD([sQuery(id+"F3.wireOp",EDGE,"E6.4.0.5")])],"isStart":false})});
            var Q91;
            Q91=makeQuery(id+"F4.boolean.opBoolean","COPY",EDGE,{"derivedFrom":makeQuery(id+"F4.opExtrude","CAP_EDGE",EDGE,{"disambiguationData":[OSD([sQuery(id+"F3.wireOp",EDGE,"E6.1.0.4")])],"isStart":false})});
            var Q92;
            Q92=makeQuery(id+"F4.boolean.opBoolean","COPY",EDGE,{"derivedFrom":makeQuery(id+"F4.opExtrude","CAP_EDGE",EDGE,{"disambiguationData":[OSD([sQuery(id+"F3.wireOp",EDGE,"E6.2.0.2")])],"isStart":false})});
            var Q93;
            Q93=makeQuery(id+"F4.boolean.opBoolean","COPY",EDGE,{"derivedFrom":makeQuery(id+"F4.opExtrude","CAP_EDGE",EDGE,{"disambiguationData":[OSD([sQuery(id+"F3.wireOp",EDGE,"E6.2.1.5")])],"isStart":false})});
            var Q94;
            Q94=makeQuery(id+"F4.boolean.opBoolean","COPY",EDGE,{"derivedFrom":makeQuery(id+"F4.opExtrude","CAP_EDGE",EDGE,{"disambiguationData":[OSD([sQuery(id+"F3.wireOp",EDGE,"E6.3.1.3")])],"isStart":false})});
            var Q95;
            Q95=makeQuery(id+"F4.boolean.opBoolean","COPY",EDGE,{"derivedFrom":makeQuery(id+"F4.opExtrude","CAP_EDGE",EDGE,{"disambiguationData":[OSD([sQuery(id+"F3.wireOp",EDGE,"E6.4.1.0")])],"isStart":false})});
            var Q96;
            Q96=makeQuery(id+"F4.boolean.opBoolean","COPY",EDGE,{"derivedFrom":makeQuery(id+"F4.opExtrude","CAP_EDGE",EDGE,{"disambiguationData":[OSD([sQuery(id+"F3.wireOp",EDGE,"E6.0.1.4")])],"isStart":true})});
            var Q97;
            Q97=makeQuery(id+"F4.boolean.opBoolean","COPY",EDGE,{"derivedFrom":makeQuery(id+"F4.opExtrude","CAP_EDGE",EDGE,{"disambiguationData":[OSD([sQuery(id+"F3.wireOp",EDGE,"E5.1.0")])],"isStart":true})});
            var Q98;
            Q98=makeQuery(id+"F4.boolean.opBoolean","COPY",EDGE,{"derivedFrom":makeQuery(id+"F4.opExtrude","CAP_EDGE",EDGE,{"disambiguationData":[OSD([sQuery(id+"F3.wireOp",EDGE,"E6.0.1.4")])],"isStart":false})});
            var Q99;
            Q99=makeQuery(id+"F4.boolean.opBoolean","COPY",EDGE,{"derivedFrom":makeQuery(id+"F4.opExtrude","CAP_EDGE",EDGE,{"disambiguationData":[OSD([sQuery(id+"F3.wireOp",EDGE,"E5.1.0")])],"isStart":false})});
            fillet(context, id + "F7", {"entities" : qUnion([Q0, Q1, Q2, Q3, Q4, Q5, Q6, Q7, Q8, Q9, Q10, Q11, Q12, Q13, Q14, Q15, Q16, Q17, Q18, Q19, Q20, Q21, Q22, Q23, Q24, Q25, Q26, Q27, Q28, Q29, Q30, Q31, Q32, Q33, Q34, Q35, Q36, Q37, Q38, Q39, Q40, Q41, Q42, Q43, Q44, Q45, Q46, Q47, Q48, Q49, Q50, Q51, Q52, Q53, Q54, Q55, Q56, Q57, Q58, Q59, Q60, Q61, Q62, Q63, Q64, Q65, Q66, Q67, Q68, Q69, Q70, Q71, Q72, Q73, Q74, Q75, Q76, Q77, Q78, Q79, Q80, Q81, Q82, Q83, Q84, Q85, Q86, Q87, Q88, Q89, Q90, Q91, Q92, Q93, Q94, Q95, Q96, Q97, Q98, Q99]), "radius" : 1.27 * mm, "tangentPropagation" : true, "allowEdgeOverflow" : false});
        }
        {
            var Q0;
            Q0=makeQuery(id+"F1.opExtrude","CAP_EDGE",EDGE,{"disambiguationData":[OSD([sQuery(id+"F0.wireOp",EDGE,"E0.top")])],"isStart":true});
            chamfer(context, id + "F8", {"entities" : qUnion([Q0]), "width" : 0.76 * mm, "tangentPropagation" : true});
        }
        {
            var Q0;
            Q0=makeQuery(id+"F1.opExtrude","SWEPT_FACE",FACE,{"disambiguationData":[OSD([sQuery(id+"F0.wireOp",EDGE,"E0.top")])]});
            var sketch = newSketch(context, id + "F9", { "sketchPlane" : qUnion([Q0])});
            skText(sketch, "E7", { "text": ".38 SPECIAL /.357 MAGNUM", "fontName": "OpenSans-Bold.ttf"});
            const initialGuessF9  = {"E7": [-0.0795, 0.00503, 1, 0, 0.00864]};
            skSetInitialGuess(sketch, initialGuessF9);
            skSolve(sketch);
        }
        {
            var Q0;
            Q0 = qSketchRegion(id + "F9", true);
            extrude(context, id + "F10", {"entities" : qUnion([Q0]), "operationType" : NewBodyOperationType.ADD, "depth" : 0.5 * mm, "offsetDistance" : 25.4 * mm});
        }
        {
            var Q0;
            Q0=makeQuery(id+"F10.opExtrude","CAP_FACE",FACE,{"disambiguationData":[OSD([sQuery(id+"F9.wireOp",EDGE,"E7.sketch_text.stroke-0"),sQuery(id+"F9.wireOp",EDGE,"E7.sketch_text.stroke-1"),sQuery(id+"F9.wireOp",EDGE,"E7.sketch_text.stroke-2"),sQuery(id+"F9.wireOp",EDGE,"E7.sketch_text.stroke-3"),sQuery(id+"F9.wireOp",EDGE,"E7.sketch_text.stroke-4"),sQuery(id+"F9.wireOp",EDGE,"E7.sketch_text.stroke-5"),sQuery(id+"F9.wireOp",EDGE,"E7.sketch_text.stroke-6"),sQuery(id+"F9.wireOp",EDGE,"E7.sketch_text.stroke-7")])],"isStart":false});
            var Q1;
            Q1=makeQuery(id+"F10.opExtrude","CAP_FACE",FACE,{"disambiguationData":[OSD([sQuery(id+"F9.wireOp",EDGE,"E7.sketch_text.stroke-8"),sQuery(id+"F9.wireOp",EDGE,"E7.sketch_text.stroke-9"),sQuery(id+"F9.wireOp",EDGE,"E7.sketch_text.stroke-10"),sQuery(id+"F9.wireOp",EDGE,"E7.sketch_text.stroke-11"),sQuery(id+"F9.wireOp",EDGE,"E7.sketch_text.stroke-12"),sQuery(id+"F9.wireOp",EDGE,"E7.sketch_text.stroke-13"),sQuery(id+"F9.wireOp",EDGE,"E7.sketch_text.stroke-14"),sQuery(id+"F9.wireOp",EDGE,"E7.sketch_text.stroke-15"),sQuery(id+"F9.wireOp",EDGE,"E7.sketch_text.stroke-16"),sQuery(id+"F9.wireOp",EDGE,"E7.sketch_text.stroke-17"),sQuery(id+"F9.wireOp",EDGE,"E7.sketch_text.stroke-18"),sQuery(id+"F9.wireOp",EDGE,"E7.sketch_text.stroke-19"),sQuery(id+"F9.wireOp",EDGE,"E7.sketch_text.stroke-20"),sQuery(id+"F9.wireOp",EDGE,"E7.sketch_text.stroke-21"),sQuery(id+"F9.wireOp",EDGE,"E7.sketch_text.stroke-22"),sQuery(id+"F9.wireOp",EDGE,"E7.sketch_text.stroke-23"),sQuery(id+"F9.wireOp",EDGE,"E7.sketch_text.stroke-24"),sQuery(id+"F9.wireOp",EDGE,"E7.sketch_text.stroke-25"),sQuery(id+"F9.wireOp",EDGE,"E7.sketch_text.stroke-26"),sQuery(id+"F9.wireOp",EDGE,"E7.sketch_text.stroke-27"),sQuery(id+"F9.wireOp",EDGE,"E7.sketch_text.stroke-28"),sQuery(id+"F9.wireOp",EDGE,"E7.sketch_text.stroke-29"),sQuery(id+"F9.wireOp",EDGE,"E7.sketch_text.stroke-30"),sQuery(id+"F9.wireOp",EDGE,"E7.sketch_text.stroke-31"),sQuery(id+"F9.wireOp",EDGE,"E7.sketch_text.stroke-32"),sQuery(id+"F9.wireOp",EDGE,"E7.sketch_text.stroke-33"),sQuery(id+"F9.wireOp",EDGE,"E7.sketch_text.stroke-34")])],"isStart":false});
            var Q2;
            Q2=makeQuery(id+"F10.opExtrude","CAP_FACE",FACE,{"disambiguationData":[OSD([sQuery(id+"F9.wireOp",EDGE,"E7.sketch_text.stroke-35"),sQuery(id+"F9.wireOp",EDGE,"E7.sketch_text.stroke-36"),sQuery(id+"F9.wireOp",EDGE,"E7.sketch_text.stroke-37"),sQuery(id+"F9.wireOp",EDGE,"E7.sketch_text.stroke-38"),sQuery(id+"F9.wireOp",EDGE,"E7.sketch_text.stroke-39"),sQuery(id+"F9.wireOp",EDGE,"E7.sketch_text.stroke-40"),sQuery(id+"F9.wireOp",EDGE,"E7.sketch_text.stroke-41"),sQuery(id+"F9.wireOp",EDGE,"E7.sketch_text.stroke-42"),sQuery(id+"F9.wireOp",EDGE,"E7.sketch_text.stroke-43"),sQuery(id+"F9.wireOp",EDGE,"E7.sketch_text.stroke-44"),sQuery(id+"F9.wireOp",EDGE,"E7.sketch_text.stroke-45"),sQuery(id+"F9.wireOp",EDGE,"E7.sketch_text.stroke-46"),sQuery(id+"F9.wireOp",EDGE,"E7.sketch_text.stroke-47"),sQuery(id+"F9.wireOp",EDGE,"E7.sketch_text.stroke-48"),sQuery(id+"F9.wireOp",EDGE,"E7.sketch_text.stroke-49"),sQuery(id+"F9.wireOp",EDGE,"E7.sketch_text.stroke-50"),sQuery(id+"F9.wireOp",EDGE,"E7.sketch_text.stroke-51"),sQuery(id+"F9.wireOp",EDGE,"E7.sketch_text.stroke-52"),sQuery(id+"F9.wireOp",EDGE,"E7.sketch_text.stroke-53"),sQuery(id+"F9.wireOp",EDGE,"E7.sketch_text.stroke-54"),sQuery(id+"F9.wireOp",EDGE,"E7.sketch_text.stroke-55"),sQuery(id+"F9.wireOp",EDGE,"E7.sketch_text.stroke-56"),sQuery(id+"F9.wireOp",EDGE,"E7.sketch_text.stroke-57"),sQuery(id+"F9.wireOp",EDGE,"E7.sketch_text.stroke-58"),sQuery(id+"F9.wireOp",EDGE,"E7.sketch_text.stroke-59"),sQuery(id+"F9.wireOp",EDGE,"E7.sketch_text.stroke-60"),sQuery(id+"F9.wireOp",EDGE,"E7.sketch_text.stroke-61"),sQuery(id+"F9.wireOp",EDGE,"E7.sketch_text.stroke-62"),sQuery(id+"F9.wireOp",EDGE,"E7.sketch_text.stroke-63"),sQuery(id+"F9.wireOp",EDGE,"E7.sketch_text.stroke-64"),sQuery(id+"F9.wireOp",EDGE,"E7.sketch_text.stroke-65")])],"isStart":false});
            var Q3;
            Q3=makeQuery(id+"F10.opExtrude","CAP_FACE",FACE,{"disambiguationData":[OSD([sQuery(id+"F9.wireOp",EDGE,"E7.sketch_text.stroke-66"),sQuery(id+"F9.wireOp",EDGE,"E7.sketch_text.stroke-67"),sQuery(id+"F9.wireOp",EDGE,"E7.sketch_text.stroke-68"),sQuery(id+"F9.wireOp",EDGE,"E7.sketch_text.stroke-69"),sQuery(id+"F9.wireOp",EDGE,"E7.sketch_text.stroke-70"),sQuery(id+"F9.wireOp",EDGE,"E7.sketch_text.stroke-71"),sQuery(id+"F9.wireOp",EDGE,"E7.sketch_text.stroke-72"),sQuery(id+"F9.wireOp",EDGE,"E7.sketch_text.stroke-73"),sQuery(id+"F9.wireOp",EDGE,"E7.sketch_text.stroke-74"),sQuery(id+"F9.wireOp",EDGE,"E7.sketch_text.stroke-75"),sQuery(id+"F9.wireOp",EDGE,"E7.sketch_text.stroke-76"),sQuery(id+"F9.wireOp",EDGE,"E7.sketch_text.stroke-77"),sQuery(id+"F9.wireOp",EDGE,"E7.sketch_text.stroke-78"),sQuery(id+"F9.wireOp",EDGE,"E7.sketch_text.stroke-79"),sQuery(id+"F9.wireOp",EDGE,"E7.sketch_text.stroke-80"),sQuery(id+"F9.wireOp",EDGE,"E7.sketch_text.stroke-81"),sQuery(id+"F9.wireOp",EDGE,"E7.sketch_text.stroke-82"),sQuery(id+"F9.wireOp",EDGE,"E7.sketch_text.stroke-83"),sQuery(id+"F9.wireOp",EDGE,"E7.sketch_text.stroke-84"),sQuery(id+"F9.wireOp",EDGE,"E7.sketch_text.stroke-85"),sQuery(id+"F9.wireOp",EDGE,"E7.sketch_text.stroke-86"),sQuery(id+"F9.wireOp",EDGE,"E7.sketch_text.stroke-87"),sQuery(id+"F9.wireOp",EDGE,"E7.sketch_text.stroke-88"),sQuery(id+"F9.wireOp",EDGE,"E7.sketch_text.stroke-89"),sQuery(id+"F9.wireOp",EDGE,"E7.sketch_text.stroke-90"),sQuery(id+"F9.wireOp",EDGE,"E7.sketch_text.stroke-91"),sQuery(id+"F9.wireOp",EDGE,"E7.sketch_text.stroke-92"),sQuery(id+"F9.wireOp",EDGE,"E7.sketch_text.stroke-93")])],"isStart":false});
            var Q4;
            Q4=makeQuery(id+"F10.opExtrude","CAP_FACE",FACE,{"disambiguationData":[OSD([sQuery(id+"F9.wireOp",EDGE,"E7.sketch_text.stroke-94"),sQuery(id+"F9.wireOp",EDGE,"E7.sketch_text.stroke-95"),sQuery(id+"F9.wireOp",EDGE,"E7.sketch_text.stroke-96"),sQuery(id+"F9.wireOp",EDGE,"E7.sketch_text.stroke-97"),sQuery(id+"F9.wireOp",EDGE,"E7.sketch_text.stroke-98"),sQuery(id+"F9.wireOp",EDGE,"E7.sketch_text.stroke-99"),sQuery(id+"F9.wireOp",EDGE,"E7.sketch_text.stroke-100"),sQuery(id+"F9.wireOp",EDGE,"E7.sketch_text.stroke-101"),sQuery(id+"F9.wireOp",EDGE,"E7.sketch_text.stroke-102"),sQuery(id+"F9.wireOp",EDGE,"E7.sketch_text.stroke-103"),sQuery(id+"F9.wireOp",EDGE,"E7.sketch_text.stroke-104"),sQuery(id+"F9.wireOp",EDGE,"E7.sketch_text.stroke-105"),sQuery(id+"F9.wireOp",EDGE,"E7.sketch_text.stroke-106"),sQuery(id+"F9.wireOp",EDGE,"E7.sketch_text.stroke-107"),sQuery(id+"F9.wireOp",EDGE,"E7.sketch_text.stroke-108"),sQuery(id+"F9.wireOp",EDGE,"E7.sketch_text.stroke-109")])],"isStart":false});
            var Q5;
            Q5=makeQuery(id+"F10.opExtrude","CAP_FACE",FACE,{"disambiguationData":[OSD([sQuery(id+"F9.wireOp",EDGE,"E7.sketch_text.stroke-110"),sQuery(id+"F9.wireOp",EDGE,"E7.sketch_text.stroke-111"),sQuery(id+"F9.wireOp",EDGE,"E7.sketch_text.stroke-112"),sQuery(id+"F9.wireOp",EDGE,"E7.sketch_text.stroke-113"),sQuery(id+"F9.wireOp",EDGE,"E7.sketch_text.stroke-114"),sQuery(id+"F9.wireOp",EDGE,"E7.sketch_text.stroke-115"),sQuery(id+"F9.wireOp",EDGE,"E7.sketch_text.stroke-116"),sQuery(id+"F9.wireOp",EDGE,"E7.sketch_text.stroke-117"),sQuery(id+"F9.wireOp",EDGE,"E7.sketch_text.stroke-118"),sQuery(id+"F9.wireOp",EDGE,"E7.sketch_text.stroke-119"),sQuery(id+"F9.wireOp",EDGE,"E7.sketch_text.stroke-120"),sQuery(id+"F9.wireOp",EDGE,"E7.sketch_text.stroke-121")])],"isStart":false});
            var Q6;
            Q6=makeQuery(id+"F10.opExtrude","CAP_FACE",FACE,{"disambiguationData":[OSD([sQuery(id+"F9.wireOp",EDGE,"E7.sketch_text.stroke-137"),sQuery(id+"F9.wireOp",EDGE,"E7.sketch_text.stroke-138"),sQuery(id+"F9.wireOp",EDGE,"E7.sketch_text.stroke-139"),sQuery(id+"F9.wireOp",EDGE,"E7.sketch_text.stroke-140")])],"isStart":false});
            var Q7;
            Q7=makeQuery(id+"F10.opExtrude","CAP_FACE",FACE,{"disambiguationData":[OSD([sQuery(id+"F9.wireOp",EDGE,"E7.sketch_text.stroke-122"),sQuery(id+"F9.wireOp",EDGE,"E7.sketch_text.stroke-123"),sQuery(id+"F9.wireOp",EDGE,"E7.sketch_text.stroke-124"),sQuery(id+"F9.wireOp",EDGE,"E7.sketch_text.stroke-125"),sQuery(id+"F9.wireOp",EDGE,"E7.sketch_text.stroke-126"),sQuery(id+"F9.wireOp",EDGE,"E7.sketch_text.stroke-127"),sQuery(id+"F9.wireOp",EDGE,"E7.sketch_text.stroke-128"),sQuery(id+"F9.wireOp",EDGE,"E7.sketch_text.stroke-129"),sQuery(id+"F9.wireOp",EDGE,"E7.sketch_text.stroke-130"),sQuery(id+"F9.wireOp",EDGE,"E7.sketch_text.stroke-131"),sQuery(id+"F9.wireOp",EDGE,"E7.sketch_text.stroke-132"),sQuery(id+"F9.wireOp",EDGE,"E7.sketch_text.stroke-133"),sQuery(id+"F9.wireOp",EDGE,"E7.sketch_text.stroke-134"),sQuery(id+"F9.wireOp",EDGE,"E7.sketch_text.stroke-135"),sQuery(id+"F9.wireOp",EDGE,"E7.sketch_text.stroke-136")])],"isStart":false});
            fillet(context, id + "F11", {"entities" : qUnion([Q0, Q1, Q2, Q3, Q4, Q5, Q6, Q7]), "radius" : 0.25 * mm, "tangentPropagation" : true, "allowEdgeOverflow" : false});
        }
        {
            var Q0;
            Q0=makeQuery(id+"F10.opExtrude","CAP_EDGE",EDGE,{"disambiguationData":[OSD([sQuery(id+"F9.wireOp",EDGE,"E7.sketch_text.stroke-145")])],"isStart":false});
            var Q1;
            Q1=makeQuery(id+"F10.opExtrude","CAP_EDGE",EDGE,{"disambiguationData":[OSD([sQuery(id+"F9.wireOp",EDGE,"E7.sketch_text.stroke-146")])],"isStart":false});
            var Q2;
            Q2=makeQuery(id+"F10.opExtrude","CAP_EDGE",EDGE,{"disambiguationData":[OSD([sQuery(id+"F9.wireOp",EDGE,"E7.sketch_text.stroke-147")])],"isStart":false});
            var Q3;
            Q3=makeQuery(id+"F10.opExtrude","CAP_EDGE",EDGE,{"disambiguationData":[OSD([sQuery(id+"F9.wireOp",EDGE,"E7.sketch_text.stroke-148")])],"isStart":false});
            var Q4;
            Q4=makeQuery(id+"F10.opExtrude","CAP_EDGE",EDGE,{"disambiguationData":[OSD([sQuery(id+"F9.wireOp",EDGE,"E7.sketch_text.stroke-141")])],"isStart":false});
            var Q5;
            Q5=makeQuery(id+"F10.opExtrude","CAP_EDGE",EDGE,{"disambiguationData":[OSD([sQuery(id+"F9.wireOp",EDGE,"E7.sketch_text.stroke-142")])],"isStart":false});
            var Q6;
            Q6=makeQuery(id+"F10.opExtrude","CAP_EDGE",EDGE,{"disambiguationData":[OSD([sQuery(id+"F9.wireOp",EDGE,"E7.sketch_text.stroke-143")])],"isStart":false});
            var Q7;
            Q7=makeQuery(id+"F10.opExtrude","CAP_EDGE",EDGE,{"disambiguationData":[OSD([sQuery(id+"F9.wireOp",EDGE,"E7.sketch_text.stroke-144")])],"isStart":false});
            var Q8;
            Q8=makeQuery(id+"F10.opExtrude","CAP_FACE",FACE,{"disambiguationData":[OSD([sQuery(id+"F9.wireOp",EDGE,"E7.sketch_text.stroke-153"),sQuery(id+"F9.wireOp",EDGE,"E7.sketch_text.stroke-154"),sQuery(id+"F9.wireOp",EDGE,"E7.sketch_text.stroke-155"),sQuery(id+"F9.wireOp",EDGE,"E7.sketch_text.stroke-156"),sQuery(id+"F9.wireOp",EDGE,"E7.sketch_text.stroke-157"),sQuery(id+"F9.wireOp",EDGE,"E7.sketch_text.stroke-158")])],"isStart":false});
            var Q9;
            Q9=makeQuery(id+"F10.opExtrude","CAP_FACE",FACE,{"disambiguationData":[OSD([sQuery(id+"F9.wireOp",EDGE,"E7.sketch_text.stroke-159"),sQuery(id+"F9.wireOp",EDGE,"E7.sketch_text.stroke-160"),sQuery(id+"F9.wireOp",EDGE,"E7.sketch_text.stroke-161"),sQuery(id+"F9.wireOp",EDGE,"E7.sketch_text.stroke-162")])],"isStart":false});
            var Q10;
            Q10=makeQuery(id+"F10.opExtrude","CAP_FACE",FACE,{"disambiguationData":[OSD([sQuery(id+"F9.wireOp",EDGE,"E7.sketch_text.stroke-163"),sQuery(id+"F9.wireOp",EDGE,"E7.sketch_text.stroke-164"),sQuery(id+"F9.wireOp",EDGE,"E7.sketch_text.stroke-165"),sQuery(id+"F9.wireOp",EDGE,"E7.sketch_text.stroke-166"),sQuery(id+"F9.wireOp",EDGE,"E7.sketch_text.stroke-167"),sQuery(id+"F9.wireOp",EDGE,"E7.sketch_text.stroke-168"),sQuery(id+"F9.wireOp",EDGE,"E7.sketch_text.stroke-169"),sQuery(id+"F9.wireOp",EDGE,"E7.sketch_text.stroke-170")])],"isStart":false});
            var Q11;
            Q11=makeQuery(id+"F10.opExtrude","CAP_FACE",FACE,{"disambiguationData":[OSD([sQuery(id+"F9.wireOp",EDGE,"E7.sketch_text.stroke-171"),sQuery(id+"F9.wireOp",EDGE,"E7.sketch_text.stroke-172"),sQuery(id+"F9.wireOp",EDGE,"E7.sketch_text.stroke-173"),sQuery(id+"F9.wireOp",EDGE,"E7.sketch_text.stroke-174"),sQuery(id+"F9.wireOp",EDGE,"E7.sketch_text.stroke-175"),sQuery(id+"F9.wireOp",EDGE,"E7.sketch_text.stroke-176"),sQuery(id+"F9.wireOp",EDGE,"E7.sketch_text.stroke-177"),sQuery(id+"F9.wireOp",EDGE,"E7.sketch_text.stroke-178"),sQuery(id+"F9.wireOp",EDGE,"E7.sketch_text.stroke-179"),sQuery(id+"F9.wireOp",EDGE,"E7.sketch_text.stroke-180"),sQuery(id+"F9.wireOp",EDGE,"E7.sketch_text.stroke-181"),sQuery(id+"F9.wireOp",EDGE,"E7.sketch_text.stroke-182"),sQuery(id+"F9.wireOp",EDGE,"E7.sketch_text.stroke-183"),sQuery(id+"F9.wireOp",EDGE,"E7.sketch_text.stroke-184"),sQuery(id+"F9.wireOp",EDGE,"E7.sketch_text.stroke-185"),sQuery(id+"F9.wireOp",EDGE,"E7.sketch_text.stroke-186"),sQuery(id+"F9.wireOp",EDGE,"E7.sketch_text.stroke-187"),sQuery(id+"F9.wireOp",EDGE,"E7.sketch_text.stroke-188"),sQuery(id+"F9.wireOp",EDGE,"E7.sketch_text.stroke-189"),sQuery(id+"F9.wireOp",EDGE,"E7.sketch_text.stroke-190"),sQuery(id+"F9.wireOp",EDGE,"E7.sketch_text.stroke-191"),sQuery(id+"F9.wireOp",EDGE,"E7.sketch_text.stroke-192"),sQuery(id+"F9.wireOp",EDGE,"E7.sketch_text.stroke-193"),sQuery(id+"F9.wireOp",EDGE,"E7.sketch_text.stroke-194"),sQuery(id+"F9.wireOp",EDGE,"E7.sketch_text.stroke-195"),sQuery(id+"F9.wireOp",EDGE,"E7.sketch_text.stroke-196"),sQuery(id+"F9.wireOp",EDGE,"E7.sketch_text.stroke-197")])],"isStart":false});
            var Q12;
            Q12=makeQuery(id+"F10.opExtrude","CAP_FACE",FACE,{"disambiguationData":[OSD([sQuery(id+"F9.wireOp",EDGE,"E7.sketch_text.stroke-198"),sQuery(id+"F9.wireOp",EDGE,"E7.sketch_text.stroke-199"),sQuery(id+"F9.wireOp",EDGE,"E7.sketch_text.stroke-200"),sQuery(id+"F9.wireOp",EDGE,"E7.sketch_text.stroke-201"),sQuery(id+"F9.wireOp",EDGE,"E7.sketch_text.stroke-202"),sQuery(id+"F9.wireOp",EDGE,"E7.sketch_text.stroke-203"),sQuery(id+"F9.wireOp",EDGE,"E7.sketch_text.stroke-204"),sQuery(id+"F9.wireOp",EDGE,"E7.sketch_text.stroke-205"),sQuery(id+"F9.wireOp",EDGE,"E7.sketch_text.stroke-206"),sQuery(id+"F9.wireOp",EDGE,"E7.sketch_text.stroke-207"),sQuery(id+"F9.wireOp",EDGE,"E7.sketch_text.stroke-208"),sQuery(id+"F9.wireOp",EDGE,"E7.sketch_text.stroke-209"),sQuery(id+"F9.wireOp",EDGE,"E7.sketch_text.stroke-210"),sQuery(id+"F9.wireOp",EDGE,"E7.sketch_text.stroke-211"),sQuery(id+"F9.wireOp",EDGE,"E7.sketch_text.stroke-212"),sQuery(id+"F9.wireOp",EDGE,"E7.sketch_text.stroke-213"),sQuery(id+"F9.wireOp",EDGE,"E7.sketch_text.stroke-214"),sQuery(id+"F9.wireOp",EDGE,"E7.sketch_text.stroke-215"),sQuery(id+"F9.wireOp",EDGE,"E7.sketch_text.stroke-216"),sQuery(id+"F9.wireOp",EDGE,"E7.sketch_text.stroke-217")])],"isStart":false});
            var Q13;
            Q13=makeQuery(id+"F10.opExtrude","CAP_FACE",FACE,{"disambiguationData":[OSD([sQuery(id+"F9.wireOp",EDGE,"E7.sketch_text.stroke-218"),sQuery(id+"F9.wireOp",EDGE,"E7.sketch_text.stroke-219"),sQuery(id+"F9.wireOp",EDGE,"E7.sketch_text.stroke-220"),sQuery(id+"F9.wireOp",EDGE,"E7.sketch_text.stroke-221"),sQuery(id+"F9.wireOp",EDGE,"E7.sketch_text.stroke-222"),sQuery(id+"F9.wireOp",EDGE,"E7.sketch_text.stroke-223"),sQuery(id+"F9.wireOp",EDGE,"E7.sketch_text.stroke-224")])],"isStart":false});
            var Q14;
            Q14=makeQuery(id+"F10.opExtrude","CAP_FACE",FACE,{"disambiguationData":[OSD([sQuery(id+"F9.wireOp",EDGE,"E7.sketch_text.stroke-225"),sQuery(id+"F9.wireOp",EDGE,"E7.sketch_text.stroke-226"),sQuery(id+"F9.wireOp",EDGE,"E7.sketch_text.stroke-227"),sQuery(id+"F9.wireOp",EDGE,"E7.sketch_text.stroke-228"),sQuery(id+"F9.wireOp",EDGE,"E7.sketch_text.stroke-229"),sQuery(id+"F9.wireOp",EDGE,"E7.sketch_text.stroke-230"),sQuery(id+"F9.wireOp",EDGE,"E7.sketch_text.stroke-231"),sQuery(id+"F9.wireOp",EDGE,"E7.sketch_text.stroke-232"),sQuery(id+"F9.wireOp",EDGE,"E7.sketch_text.stroke-233"),sQuery(id+"F9.wireOp",EDGE,"E7.sketch_text.stroke-234"),sQuery(id+"F9.wireOp",EDGE,"E7.sketch_text.stroke-235"),sQuery(id+"F9.wireOp",EDGE,"E7.sketch_text.stroke-236"),sQuery(id+"F9.wireOp",EDGE,"E7.sketch_text.stroke-237"),sQuery(id+"F9.wireOp",EDGE,"E7.sketch_text.stroke-238"),sQuery(id+"F9.wireOp",EDGE,"E7.sketch_text.stroke-239"),sQuery(id+"F9.wireOp",EDGE,"E7.sketch_text.stroke-240"),sQuery(id+"F9.wireOp",EDGE,"E7.sketch_text.stroke-241"),sQuery(id+"F9.wireOp",EDGE,"E7.sketch_text.stroke-242"),sQuery(id+"F9.wireOp",EDGE,"E7.sketch_text.stroke-243")])],"isStart":false});
            var Q15;
            Q15=makeQuery(id+"F10.opExtrude","CAP_FACE",FACE,{"disambiguationData":[OSD([sQuery(id+"F9.wireOp",EDGE,"E7.sketch_text.stroke-256"),sQuery(id+"F9.wireOp",EDGE,"E7.sketch_text.stroke-257"),sQuery(id+"F9.wireOp",EDGE,"E7.sketch_text.stroke-258"),sQuery(id+"F9.wireOp",EDGE,"E7.sketch_text.stroke-259"),sQuery(id+"F9.wireOp",EDGE,"E7.sketch_text.stroke-260"),sQuery(id+"F9.wireOp",EDGE,"E7.sketch_text.stroke-261"),sQuery(id+"F9.wireOp",EDGE,"E7.sketch_text.stroke-262"),sQuery(id+"F9.wireOp",EDGE,"E7.sketch_text.stroke-263"),sQuery(id+"F9.wireOp",EDGE,"E7.sketch_text.stroke-264"),sQuery(id+"F9.wireOp",EDGE,"E7.sketch_text.stroke-265"),sQuery(id+"F9.wireOp",EDGE,"E7.sketch_text.stroke-266"),sQuery(id+"F9.wireOp",EDGE,"E7.sketch_text.stroke-267"),sQuery(id+"F9.wireOp",EDGE,"E7.sketch_text.stroke-268"),sQuery(id+"F9.wireOp",EDGE,"E7.sketch_text.stroke-269"),sQuery(id+"F9.wireOp",EDGE,"E7.sketch_text.stroke-270"),sQuery(id+"F9.wireOp",EDGE,"E7.sketch_text.stroke-271"),sQuery(id+"F9.wireOp",EDGE,"E7.sketch_text.stroke-272"),sQuery(id+"F9.wireOp",EDGE,"E7.sketch_text.stroke-273"),sQuery(id+"F9.wireOp",EDGE,"E7.sketch_text.stroke-274")])],"isStart":false});
            var Q16;
            Q16=makeQuery(id+"F10.opExtrude","CAP_FACE",FACE,{"disambiguationData":[OSD([sQuery(id+"F9.wireOp",EDGE,"E7.sketch_text.stroke-275"),sQuery(id+"F9.wireOp",EDGE,"E7.sketch_text.stroke-276"),sQuery(id+"F9.wireOp",EDGE,"E7.sketch_text.stroke-277"),sQuery(id+"F9.wireOp",EDGE,"E7.sketch_text.stroke-278"),sQuery(id+"F9.wireOp",EDGE,"E7.sketch_text.stroke-279"),sQuery(id+"F9.wireOp",EDGE,"E7.sketch_text.stroke-280"),sQuery(id+"F9.wireOp",EDGE,"E7.sketch_text.stroke-281"),sQuery(id+"F9.wireOp",EDGE,"E7.sketch_text.stroke-282"),sQuery(id+"F9.wireOp",EDGE,"E7.sketch_text.stroke-283"),sQuery(id+"F9.wireOp",EDGE,"E7.sketch_text.stroke-284"),sQuery(id+"F9.wireOp",EDGE,"E7.sketch_text.stroke-285"),sQuery(id+"F9.wireOp",EDGE,"E7.sketch_text.stroke-286"),sQuery(id+"F9.wireOp",EDGE,"E7.sketch_text.stroke-287"),sQuery(id+"F9.wireOp",EDGE,"E7.sketch_text.stroke-288")])],"isStart":false});
            var Q17;
            Q17=makeQuery(id+"F10.opExtrude","CAP_FACE",FACE,{"disambiguationData":[OSD([sQuery(id+"F9.wireOp",EDGE,"E7.sketch_text.stroke-289"),sQuery(id+"F9.wireOp",EDGE,"E7.sketch_text.stroke-290"),sQuery(id+"F9.wireOp",EDGE,"E7.sketch_text.stroke-291"),sQuery(id+"F9.wireOp",EDGE,"E7.sketch_text.stroke-292"),sQuery(id+"F9.wireOp",EDGE,"E7.sketch_text.stroke-293"),sQuery(id+"F9.wireOp",EDGE,"E7.sketch_text.stroke-294"),sQuery(id+"F9.wireOp",EDGE,"E7.sketch_text.stroke-295"),sQuery(id+"F9.wireOp",EDGE,"E7.sketch_text.stroke-296"),sQuery(id+"F9.wireOp",EDGE,"E7.sketch_text.stroke-297"),sQuery(id+"F9.wireOp",EDGE,"E7.sketch_text.stroke-298"),sQuery(id+"F9.wireOp",EDGE,"E7.sketch_text.stroke-299"),sQuery(id+"F9.wireOp",EDGE,"E7.sketch_text.stroke-300"),sQuery(id+"F9.wireOp",EDGE,"E7.sketch_text.stroke-301"),sQuery(id+"F9.wireOp",EDGE,"E7.sketch_text.stroke-302"),sQuery(id+"F9.wireOp",EDGE,"E7.sketch_text.stroke-303")])],"isStart":false});
            var Q18;
            Q18=makeQuery(id+"F10.opExtrude","CAP_FACE",FACE,{"disambiguationData":[OSD([sQuery(id+"F9.wireOp",EDGE,"E7.sketch_text.stroke-304"),sQuery(id+"F9.wireOp",EDGE,"E7.sketch_text.stroke-305"),sQuery(id+"F9.wireOp",EDGE,"E7.sketch_text.stroke-306"),sQuery(id+"F9.wireOp",EDGE,"E7.sketch_text.stroke-307"),sQuery(id+"F9.wireOp",EDGE,"E7.sketch_text.stroke-308"),sQuery(id+"F9.wireOp",EDGE,"E7.sketch_text.stroke-309"),sQuery(id+"F9.wireOp",EDGE,"E7.sketch_text.stroke-310"),sQuery(id+"F9.wireOp",EDGE,"E7.sketch_text.stroke-311"),sQuery(id+"F9.wireOp",EDGE,"E7.sketch_text.stroke-312"),sQuery(id+"F9.wireOp",EDGE,"E7.sketch_text.stroke-313"),sQuery(id+"F9.wireOp",EDGE,"E7.sketch_text.stroke-314"),sQuery(id+"F9.wireOp",EDGE,"E7.sketch_text.stroke-315"),sQuery(id+"F9.wireOp",EDGE,"E7.sketch_text.stroke-316"),sQuery(id+"F9.wireOp",EDGE,"E7.sketch_text.stroke-317"),sQuery(id+"F9.wireOp",EDGE,"E7.sketch_text.stroke-318"),sQuery(id+"F9.wireOp",EDGE,"E7.sketch_text.stroke-319"),sQuery(id+"F9.wireOp",EDGE,"E7.sketch_text.stroke-320"),sQuery(id+"F9.wireOp",EDGE,"E7.sketch_text.stroke-321"),sQuery(id+"F9.wireOp",EDGE,"E7.sketch_text.stroke-322")])],"isStart":false});
            var Q19;
            Q19=makeQuery(id+"F10.opExtrude","CAP_EDGE",EDGE,{"disambiguationData":[OSD([sQuery(id+"F9.wireOp",EDGE,"E7.sketch_text.stroke-245")])],"isStart":false});
            var Q20;
            Q20=makeQuery(id+"F10.opExtrude","CAP_EDGE",EDGE,{"disambiguationData":[OSD([sQuery(id+"F9.wireOp",EDGE,"E7.sketch_text.stroke-244")])],"isStart":false});
            var Q21;
            Q21=makeQuery(id+"F10.opExtrude","CAP_EDGE",EDGE,{"disambiguationData":[OSD([sQuery(id+"F9.wireOp",EDGE,"E7.sketch_text.stroke-251")])],"isStart":false});
            var Q22;
            Q22=makeQuery(id+"F10.opExtrude","CAP_EDGE",EDGE,{"disambiguationData":[OSD([sQuery(id+"F9.wireOp",EDGE,"E7.sketch_text.stroke-250")])],"isStart":false});
            var Q23;
            Q23=makeQuery(id+"F10.opExtrude","CAP_EDGE",EDGE,{"disambiguationData":[OSD([sQuery(id+"F9.wireOp",EDGE,"E7.sketch_text.stroke-249")])],"isStart":false});
            var Q24;
            Q24=makeQuery(id+"F10.opExtrude","CAP_EDGE",EDGE,{"disambiguationData":[OSD([sQuery(id+"F9.wireOp",EDGE,"E7.sketch_text.stroke-248")])],"isStart":false});
            var Q25;
            Q25=makeQuery(id+"F10.opExtrude","CAP_EDGE",EDGE,{"disambiguationData":[OSD([sQuery(id+"F9.wireOp",EDGE,"E7.sketch_text.stroke-247")])],"isStart":false});
            var Q26;
            Q26=makeQuery(id+"F10.opExtrude","CAP_EDGE",EDGE,{"disambiguationData":[OSD([sQuery(id+"F9.wireOp",EDGE,"E7.sketch_text.stroke-246")])],"isStart":false});
            fillet(context, id + "F12", {"entities" : qUnion([Q0, Q1, Q2, Q3, Q4, Q5, Q6, Q7, Q8, Q9, Q10, Q11, Q12, Q13, Q14, Q15, Q16, Q17, Q18, Q19, Q20, Q21, Q22, Q23, Q24, Q25, Q26]), "radius" : 0.25 * mm, "tangentPropagation" : true, "allowEdgeOverflow" : false});
        }
    });
